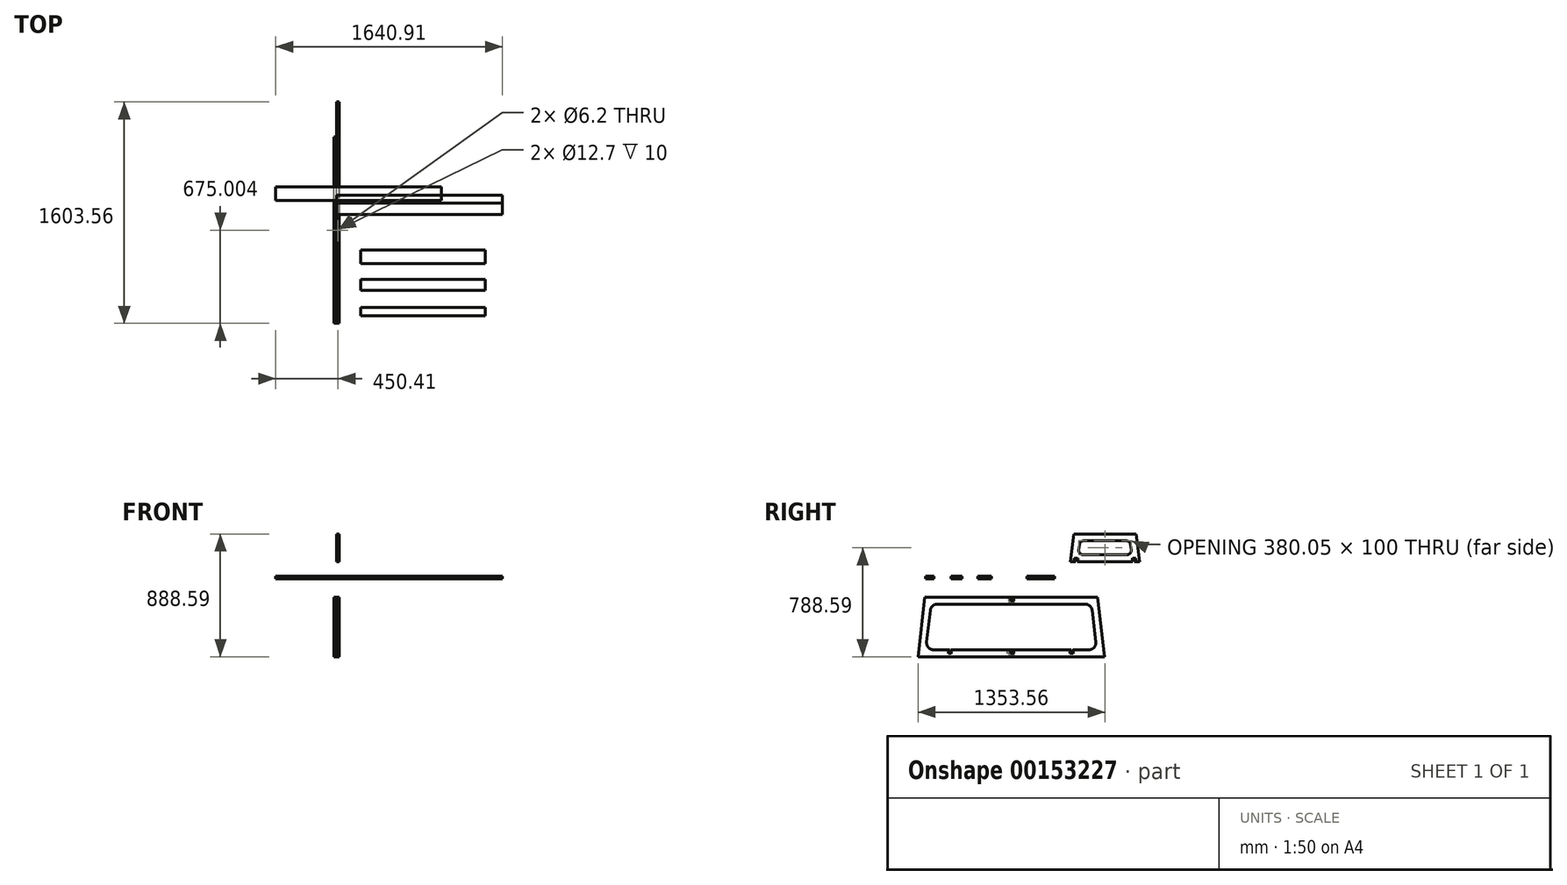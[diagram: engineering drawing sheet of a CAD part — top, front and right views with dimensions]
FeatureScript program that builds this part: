
annotation { "Feature Type Name" : "Feature", "Feature Type Description" : "" }
export const myFeature = defineFeature(function(context is Context, id is Id, definition is map)
    precondition{}
    {
        {
            var Q0;
            Q0=qCreatedBy(makeId("Top.planeOp"),FACE);
            var sketch = newSketch(context, id + "F0", { "sketchPlane" : qUnion([Q0])});
            skLineSegment(sketch, "E0.bottom", {"start": v(0, 0) * mm, "end": v(1200, 0) * mm});
            skLineSegment(sketch, "E0.top", {"start": v(0, 60) * mm, "end": v(1200, 60) * mm});
            skLineSegment(sketch, "E0.left", {"start": v(0, 0) * mm, "end": v(0, 60) * mm});
            skLineSegment(sketch, "E0.right", {"start": v(1200, 0) * mm, "end": v(1200, 60) * mm});
            skSolve(sketch);
        }
        {
            var Q0;
            Q0=makeQuery(id+"F0.imprint","IMPRINT",FACE,{"disambiguationData":[TD([[makeQuery(id+"F0.imprint","IMPRINT",EDGE,{"derivedFrom":sQuery(id+"F0.wireOp",EDGE,"E0.bottom")}),1.0]])]});
            extrude(context, id + "F1", {"entities" : qUnion([Q0]), "depth" : 19 * mm});
        }
        {
            var Q0;
            Q0=qCreatedBy(makeId("Top.planeOp"),FACE);
            var sketch = newSketch(context, id + "F2", { "sketchPlane" : qUnion([Q0])});
            skLineSegment(sketch, "E1.bottom", {"start": v(0, 0) * mm, "end": v(1200, 0) * mm});
            skLineSegment(sketch, "E1.top", {"start": v(0, -80) * mm, "end": v(1200, -80) * mm});
            skLineSegment(sketch, "E1.left", {"start": v(0, 0) * mm, "end": v(0, -80) * mm});
            skLineSegment(sketch, "E1.right", {"start": v(1200, 0) * mm, "end": v(1200, -80) * mm});
            skSolve(sketch);
        }
        {
            var Q0;
            Q0=makeQuery(id+"F2.imprint","IMPRINT",FACE,{"disambiguationData":[TD([[makeQuery(id+"F2.imprint","IMPRINT",EDGE,{"derivedFrom":sQuery(id+"F2.wireOp",EDGE,"E1.bottom")}),-1.0]])]});
            extrude(context, id + "F3", {"entities" : qUnion([Q0]), "depth" : 19 * mm});
        }
        {
            var Q0;
            Q0=qCreatedBy(makeId("Top.planeOp"),FACE);
            var sketch = newSketch(context, id + "F4", { "sketchPlane" : qUnion([Q0])});
            skLineSegment(sketch, "E2.bottom", {"start": v(-440.91, 119.85) * mm, "end": v(759.09, 119.85) * mm});
            skLineSegment(sketch, "E2.top", {"start": v(-440.91, 19.85) * mm, "end": v(759.09, 19.85) * mm});
            skLineSegment(sketch, "E2.left", {"start": v(-440.91, 119.85) * mm, "end": v(-440.91, 19.85) * mm});
            skLineSegment(sketch, "E2.right", {"start": v(759.09, 119.85) * mm, "end": v(759.09, 19.85) * mm});
            skSolve(sketch);
        }
        {
            var Q0;
            Q0=makeQuery(id+"F4.imprint","IMPRINT",FACE,{"disambiguationData":[TD([[makeQuery(id+"F4.imprint","IMPRINT",EDGE,{"derivedFrom":sQuery(id+"F4.wireOp",EDGE,"E2.bottom")}),-1.0]])]});
            extrude(context, id + "F5", {"entities" : qUnion([Q0]), "depth" : 19 * mm});
        }
        {
            var Q0;
            Q0=qCreatedBy(makeId("Right.planeOp"),FACE);
            var sketch = newSketch(context, id + "F6", { "sketchPlane" : qUnion([Q0])});
            skLineSegment(sketch, "E3", {"start": v(-819.63, -132.58) * mm, "end": v(430.37, -132.58) * mm});
            skLineSegment(sketch, "E4", {"start": v(430.37, -132.58) * mm, "end": v(480.37, -562.58) * mm});
            skLineSegment(sketch, "E5", {"start": v(480.37, -562.58) * mm, "end": v(-869.63, -562.58) * mm});
            skLineSegment(sketch, "E6", {"start": v(-869.63, -562.58) * mm, "end": v(-819.63, -132.58) * mm});
            skLineSegment(sketch, "E7.0", {"start": v(-730.58, -182.58) * mm, "end": v(341.33, -182.58) * mm});
            skLineSegment(sketch, "E7.1", {"start": v(-807, -456.8) * mm, "end": v(-780.25, -226.8) * mm});
            skLineSegment(sketch, "E7.2", {"start": v(368.07, -512.58) * mm, "end": v(-757.32, -512.58) * mm});
            skLineSegment(sketch, "E7.3", {"start": v(391, -226.8) * mm, "end": v(417.74, -456.8) * mm});
            skPoint(sketch, "E8.visualSharp", {"position": v(-775.1, -182.58) * mm});
            skArc(sketch, "E8.filletArc", {"start": v(-730.58, -182.58) * mm, "mid": v(-763.83, -195.24) * mm, "end": v(-780.25, -226.8) * mm});
            skPoint(sketch, "E9.visualSharp", {"position": v(385.85, -182.58) * mm});
            skArc(sketch, "E9.filletArc", {"start": v(391, -226.8) * mm, "mid": v(374.58, -195.24) * mm, "end": v(341.33, -182.58) * mm});
            skPoint(sketch, "E10.visualSharp", {"position": v(424.22, -512.58) * mm});
            skArc(sketch, "E10.filletArc", {"start": v(368.07, -512.58) * mm, "mid": v(405.41, -495.83) * mm, "end": v(417.74, -456.8) * mm});
            skPoint(sketch, "E11.visualSharp", {"position": v(-813.48, -512.58) * mm});
            skArc(sketch, "E11.filletArc", {"start": v(-807, -456.8) * mm, "mid": v(-794.67, -495.83) * mm, "end": v(-757.32, -512.58) * mm});
            skSolve(sketch);
        }
        {
            var Q0;
            Q0=makeQuery(id+"F6.imprint","IMPRINT",FACE,{"disambiguationData":[TD([[makeQuery(id+"F6.imprint","IMPRINT",EDGE,{"derivedFrom":sQuery(id+"F6.wireOp",EDGE,"E3")}),-1.0]])]});
            extrude(context, id + "F7", {"entities" : qUnion([Q0]), "depth" : 19 * mm});
        }
        {
            var Q0;
            Q0 = qSketchRegion(id + "F6", true);
            extrude(context, id + "F8", {"entities" : qUnion([Q0]), "oppositeDirection" : true, "depth" : 19 * mm});
        }
        {
            var Q0;
            Q0=makeQuery(id+"F7.opExtrude","SWEPT_FACE",FACE,{"disambiguationData":[OSD([sQuery(id+"F6.wireOp",EDGE,"E3")])]});
            var sketch = newSketch(context, id + "F9", { "sketchPlane" : qUnion([Q0])});
            skLineSegment(sketch, "E12", {"start": v(-59.98, -230.03) * mm, "end": v(45, -159.22) * mm});
            skLineSegment(sketch, "E13", {"start": v(45, -159.22) * mm, "end": v(55.63, -174.97) * mm});
            skLineSegment(sketch, "E14", {"start": v(55.63, -174.97) * mm, "end": v(-53.9, -248.85) * mm});
            skLineSegment(sketch, "E15", {"start": v(-53.9, -248.85) * mm, "end": v(-59.98, -230.03) * mm});
            skLineSegment(sketch, "E16", {"start": v(19, -176.76) * mm, "end": v(78.43, -176.76) * mm, "construction": true});
            skLineSegment(sketch, "E17", {"start": v(0, -212.5) * mm, "end": v(81.3, -212.5) * mm, "construction": true});
            skPoint(sketch, "E18", {"position": v(9.5, -194.63) * mm});
            skPoint(sketch, "E18.positionSnap0", {"position": v(-7.49, -194.63) * mm});
            skSolve(sketch);
        }
        {
            var Q0;
            {var subQ0=sQuery(id+"F9.wireOp",EDGE,"E12");var subQ1=sQuery(id+"F6.wireOp",EDGE,"E3");var subQ2=makeQuery(id+"F7.opExtrude","CAP_EDGE",EDGE,{"disambiguationData":[OSD([subQ1])],"isStart":true});var subQ3=makeQuery(id+"F9.imprint","INTERSECT",VERTEX,{"derivedFrom":[subQ2,subQ0]});Q0=makeQuery(id+"F9.imprint","IMPRINT",FACE,{"disambiguationData":[TD([[makeQuery(id+"F9.imprint","IMPRINT",EDGE,{"disambiguationData":[TD([[subQ3,-1.0]])],"derivedFrom":subQ0}),-1.0]])]});}
            extrude(context, id + "F10", {"entities" : qUnion([Q0]), "operationType" : NewBodyOperationType.REMOVE, "oppositeDirection" : true, "depth" : 25 * mm});
        }
        {
            var Q0;
            Q0=makeQuery(id+"F7.opExtrude","SWEPT_FACE",FACE,{"disambiguationData":[OSD([sQuery(id+"F6.wireOp",EDGE,"E7.2")])]});
            var sketch = newSketch(context, id + "F11", { "sketchPlane" : qUnion([Q0])});
            skLineSegment(sketch, "E19", {"start": v(-59.98, -227.93) * mm, "end": v(45, -157.12) * mm});
            skLineSegment(sketch, "E20", {"start": v(45, -157.12) * mm, "end": v(55.63, -172.87) * mm});
            skLineSegment(sketch, "E21", {"start": v(55.63, -172.87) * mm, "end": v(-53.9, -246.75) * mm});
            skLineSegment(sketch, "E22", {"start": v(-53.9, -246.75) * mm, "end": v(-59.98, -227.93) * mm});
            skLineSegment(sketch, "E23", {"start": v(19, -174.66) * mm, "end": v(104.14, -174.66) * mm, "construction": true});
            skLineSegment(sketch, "E24", {"start": v(0, -210.4) * mm, "end": v(81.3, -210.4) * mm, "construction": true});
            skPoint(sketch, "E25", {"position": v(9.5, -192.53) * mm});
            skPoint(sketch, "E25.positionSnap0", {"position": v(-7.49, -192.53) * mm});
            skSolve(sketch);
        }
        {
            var Q0;
            Q0 = qSketchRegion(id + "F11", true);
            extrude(context, id + "F12", {"entities" : qUnion([Q0]), "operationType" : NewBodyOperationType.REMOVE, "oppositeDirection" : true, "depth" : 25 * mm});
        }
        {
            var Q0;
            Q0=makeQuery(id+"F8.opExtrude","SWEPT_FACE",FACE,{"disambiguationData":[OSD([sQuery(id+"F6.wireOp",EDGE,"E5")])]});
            var sketch = newSketch(context, id + "F13", { "sketchPlane" : qUnion([Q0])});
            skLineSegment(sketch, "E26", {"start": v(-78.98, 159.22) * mm, "end": v(26, 230.03) * mm});
            skLineSegment(sketch, "E27", {"start": v(26, 230.03) * mm, "end": v(36.63, 214.28) * mm});
            skLineSegment(sketch, "E28", {"start": v(36.63, 214.28) * mm, "end": v(-72.9, 140.4) * mm});
            skLineSegment(sketch, "E29", {"start": v(-72.9, 140.4) * mm, "end": v(-78.98, 159.22) * mm});
            skLineSegment(sketch, "E30", {"start": v(0, 212.5) * mm, "end": v(199.93, 212.5) * mm, "construction": true});
            skLineSegment(sketch, "E31", {"start": v(-19, 176.76) * mm, "end": v(206.75, 176.76) * mm, "construction": true});
            skPoint(sketch, "E32", {"position": v(-9.5, 194.63) * mm});
            skPoint(sketch, "E32.positionSnap0", {"position": v(-26.49, 194.63) * mm});
            skSolve(sketch);
        }
        {
            var Q0;
            {var subQ0=sQuery(id+"F13.wireOp",EDGE,"016648c7-12cd-486c-9a25-a43fcb7e1467");var subQ1=sQuery(id+"F6.wireOp",EDGE,"E5");var subQ2=makeQuery(id+"F8.opExtrude","CAP_EDGE",EDGE,{"disambiguationData":[OSD([subQ1])],"isStart":false});var subQ3=makeQuery(id+"F13.imprint","INTERSECT",VERTEX,{"derivedFrom":[subQ2,subQ0]});Q0=makeQuery(id+"F13.imprint","IMPRINT",FACE,{"disambiguationData":[TD([[makeQuery(id+"F13.imprint","IMPRINT",EDGE,{"disambiguationData":[TD([[subQ3,-1.0]])],"derivedFrom":subQ0}),-1.0]])]});}
            var Q1;
            {var subQ0=sQuery(id+"F13.wireOp",EDGE,"E26");var subQ1=sQuery(id+"F6.wireOp",EDGE,"E5");var subQ2=makeQuery(id+"F8.opExtrude","CAP_EDGE",EDGE,{"disambiguationData":[OSD([subQ1])],"isStart":false});var subQ3=makeQuery(id+"F13.imprint","INTERSECT",VERTEX,{"derivedFrom":[subQ2,subQ0]});Q1=makeQuery(id+"F13.imprint","IMPRINT",FACE,{"disambiguationData":[TD([[makeQuery(id+"F13.imprint","IMPRINT",EDGE,{"disambiguationData":[TD([[subQ3,-1.0]])],"derivedFrom":subQ0}),-1.0]])]});}
            extrude(context, id + "F14", {"entities" : qUnion([Q0, Q1]), "operationType" : NewBodyOperationType.REMOVE, "oppositeDirection" : true, "depth" : 25 * mm});
        }
        {
            var Q0;
            Q0=makeQuery(id+"F8.opExtrude","SWEPT_FACE",FACE,{"disambiguationData":[OSD([sQuery(id+"F6.wireOp",EDGE,"E7.0")])]});
            var sketch = newSketch(context, id + "F15", { "sketchPlane" : qUnion([Q0])});
            skLineSegment(sketch, "E33", {"start": v(-78.98, 159.22) * mm, "end": v(26, 230.03) * mm});
            skLineSegment(sketch, "E34", {"start": v(26, 230.03) * mm, "end": v(36.63, 214.28) * mm});
            skLineSegment(sketch, "E35", {"start": v(36.63, 214.28) * mm, "end": v(-72.9, 140.4) * mm});
            skLineSegment(sketch, "E36", {"start": v(-72.9, 140.4) * mm, "end": v(-78.98, 159.22) * mm});
            skLineSegment(sketch, "E37", {"start": v(-40.65, 212.5) * mm, "end": v(0, 212.5) * mm, "construction": true});
            skLineSegment(sketch, "E38", {"start": v(-37.66, 176.76) * mm, "end": v(-19, 176.76) * mm, "construction": true});
            skPoint(sketch, "E39", {"position": v(-9.5, 194.63) * mm});
            skPoint(sketch, "E39.positionSnap0", {"position": v(-26.49, 194.63) * mm});
            skSolve(sketch);
        }
        {
            var Q0;
            {var subQ0=sQuery(id+"F15.wireOp",EDGE,"9352b724-c403-4dff-b062-4e1158279c86");var subQ1=sQuery(id+"F6.wireOp",EDGE,"E7.0");var subQ2=makeQuery(id+"F8.opExtrude","CAP_EDGE",EDGE,{"disambiguationData":[OSD([subQ1])],"isStart":false});var subQ3=makeQuery(id+"F15.imprint","INTERSECT",VERTEX,{"derivedFrom":[subQ2,subQ0]});Q0=makeQuery(id+"F15.imprint","IMPRINT",FACE,{"disambiguationData":[TD([[makeQuery(id+"F15.imprint","IMPRINT",EDGE,{"disambiguationData":[TD([[subQ3,-1.0]])],"derivedFrom":subQ0}),-1.0]])]});}
            var Q1;
            {var subQ0=sQuery(id+"F15.wireOp",EDGE,"E33");var subQ1=sQuery(id+"F6.wireOp",EDGE,"E7.0");var subQ2=makeQuery(id+"F8.opExtrude","CAP_EDGE",EDGE,{"disambiguationData":[OSD([subQ1])],"isStart":false});var subQ3=makeQuery(id+"F15.imprint","INTERSECT",VERTEX,{"derivedFrom":[subQ2,subQ0]});Q1=makeQuery(id+"F15.imprint","IMPRINT",FACE,{"disambiguationData":[TD([[makeQuery(id+"F15.imprint","IMPRINT",EDGE,{"disambiguationData":[TD([[subQ3,-1.0]])],"derivedFrom":subQ0}),-1.0]])]});}
            extrude(context, id + "F16", {"entities" : qUnion([Q0, Q1]), "operationType" : NewBodyOperationType.REMOVE, "oppositeDirection" : true, "depth" : 25 * mm});
        }
        {
            var Q0;
            {var subQ10=sQuery(id+"F6.wireOp",EDGE,"E4");var subQ11=sQuery(id+"F6.wireOp",EDGE,"E3");Q0=makeQuery(id+"F10.boolean.opBoolean","SPLIT",FACE,{"disambiguationData":[TD([makeQuery(id+"F7.opExtrude","SWEPT_FACE",FACE,{"disambiguationData":[OSD([subQ10])]})])],"derivedFrom":makeQuery(id+"F7.opExtrude","SWEPT_FACE",FACE,{"disambiguationData":[OSD([subQ11])]})});}
            var sketch = newSketch(context, id + "F17", { "sketchPlane" : qUnion([Q0])});
            skLineSegment(sketch, "E40", {"start": v(0, -212.99) * mm, "end": v(19, -176.76) * mm});
            skSolve(sketch);
        }
        {
            var Q0;
            Q0=makeQuery(id+"F7.opExtrude","SWEPT_FACE",FACE,{"disambiguationData":[OSD([sQuery(id+"F6.wireOp",EDGE,"E5")])]});
            var sketch = newSketch(context, id + "F18", { "sketchPlane" : qUnion([Q0])});
            skCircle(sketch, "E41", {"center": v(9.5, 194.63) * mm, "radius": 6.35 * mm});
            skSolve(sketch);
        }
        {
            var Q0;
            Q0=makeQuery(id+"F18.imprint","IMPRINT",FACE,{"disambiguationData":[TD([[makeQuery(id+"F18.imprint","IMPRINT",EDGE,{"derivedFrom":sQuery(id+"F18.wireOp",EDGE,"E41")}),1.0]])]});
            extrude(context, id + "F19", {"entities" : qUnion([Q0]), "operationType" : NewBodyOperationType.REMOVE, "oppositeDirection" : true, "depth" : 10 * mm});
        }
        {
            var Q0;
            Q0=makeQuery(id+"F19.boolean.opBoolean","COPY",FACE,{"derivedFrom":makeQuery(id+"F19.opExtrude","CAP_FACE",FACE,{"disambiguationData":[OSD([sQuery(id+"F18.wireOp",EDGE,"E41")])],"isStart":false})});
            var sketch = newSketch(context, id + "F20", { "sketchPlane" : qUnion([Q0])});
            skCircle(sketch, "E42", {"center": v(9.5, 194.63) * mm, "radius": 3.1 * mm});
            skSolve(sketch);
        }
        {
            var Q0;
            Q0=makeQuery(id+"F20.imprint","IMPRINT",FACE,{"disambiguationData":[TD([[makeQuery(id+"F20.imprint","IMPRINT",EDGE,{"derivedFrom":sQuery(id+"F20.wireOp",EDGE,"E42")}),1.0]])]});
            extrude(context, id + "F21", {"entities" : qUnion([Q0]), "operationType" : NewBodyOperationType.REMOVE, "endBound" : BoundingType.THROUGH_ALL, "oppositeDirection" : true, "depth" : 25 * mm});
        }
        {
            var Q0;
            Q0=makeQuery(id+"F7.opExtrude","SWEPT_FACE",FACE,{"disambiguationData":[OSD([sQuery(id+"F6.wireOp",EDGE,"E7.0")])]});
            var sketch = newSketch(context, id + "F22", { "sketchPlane" : qUnion([Q0])});
            skCircle(sketch, "E43", {"center": v(9.5, 194.63) * mm, "radius": 6.35 * mm});
            skSolve(sketch);
        }
        {
            var Q0;
            Q0=makeQuery(id+"F22.imprint","IMPRINT",FACE,{"disambiguationData":[TD([[makeQuery(id+"F22.imprint","IMPRINT",EDGE,{"derivedFrom":makeQuery(id+"F21.boolean.opBoolean","INTERSECT",EDGE,{"derivedFrom":[makeQuery(id+"F7.opExtrude","SWEPT_FACE",FACE,{"disambiguationData":[OSD([sQuery(id+"F6.wireOp",EDGE,"E7.0")])]}),makeQuery(id+"F21.opExtrude","SWEPT_FACE",FACE,{"disambiguationData":[OSD([sQuery(id+"F20.wireOp",EDGE,"E42")])]})]})}),-1.0]])]});
            extrude(context, id + "F23", {"entities" : qUnion([Q0]), "operationType" : NewBodyOperationType.REMOVE, "oppositeDirection" : true, "depth" : 10 * mm});
        }
        {
            var Q0;
            Q0=makeQuery(id+"F7.opExtrude","SWEPT_FACE",FACE,{"disambiguationData":[OSD([sQuery(id+"F6.wireOp",EDGE,"E7.0")])]});
            var sketch = newSketch(context, id + "F24", { "sketchPlane" : qUnion([Q0])});
            skCircle(sketch, "E44", {"center": v(9.5, 194.63) * mm, "radius": 6.35 * mm});
            skSolve(sketch);
        }
        {
            var Q0;
            Q0=makeQuery(id+"F24.imprint","IMPRINT",FACE,{"disambiguationData":[TD([[makeQuery(id+"F24.imprint","IMPRINT",EDGE,{"derivedFrom":sQuery(id+"F24.wireOp",EDGE,"E44")}),1.0]])]});
            extrude(context, id + "F25", {"entities" : qUnion([Q0]), "operationType" : NewBodyOperationType.REMOVE, "oppositeDirection" : true, "depth" : 10 * mm});
        }
        {
            var Q0;
            {var subQ0=sQuery(id+"F6.wireOp",EDGE,"E11.filletArc");var subQ5=sQuery(id+"F6.wireOp",EDGE,"E7.2");Q0=makeQuery(id+"F12.boolean.opBoolean","SPLIT",FACE,{"disambiguationData":[TD([makeQuery(id+"F7.opExtrude","SWEPT_FACE",FACE,{"disambiguationData":[OSD([subQ0])]})])],"derivedFrom":makeQuery(id+"F7.opExtrude","SWEPT_FACE",FACE,{"disambiguationData":[OSD([subQ5])]})});}
            var sketch = newSketch(context, id + "F26", { "sketchPlane" : qUnion([Q0])});
            skLineSegment(sketch, "E45", {"start": v(-107.43, -194.63) * mm, "end": v(150.28, -194.63) * mm, "construction": true});
            skLineSegment(sketch, "E46", {"start": v(0, -640.93) * mm, "end": v(87.61, -686.89) * mm});
            skLineSegment(sketch, "E47", {"start": v(87.61, -686.89) * mm, "end": v(87.61, -665.43) * mm});
            skLineSegment(sketch, "E48", {"start": v(87.61, -665.43) * mm, "end": v(0, -619.47) * mm});
            skLineSegment(sketch, "E49.MirrorCS", {"start": v(0, -619.47) * mm, "end": v(0, -640.93) * mm});
            skLineSegment(sketch, "E50.MirrorCS", {"start": v(-87.61, -686.89) * mm, "end": v(-87.61, -665.43) * mm});
            skLineSegment(sketch, "E51.MirrorCS", {"start": v(0, -640.93) * mm, "end": v(-87.61, -686.89) * mm});
            skLineSegment(sketch, "E52.MirrorCS", {"start": v(-87.61, -665.43) * mm, "end": v(0, -619.47) * mm});
            skLineSegment(sketch, "E53", {"start": v(0, 240.19) * mm, "end": v(19, 230.22) * mm});
            skLineSegment(sketch, "E54", {"start": v(19, 230.22) * mm, "end": v(19, 251.67) * mm});
            skLineSegment(sketch, "E55", {"start": v(19, 251.67) * mm, "end": v(0, 261.64) * mm});
            skLineSegment(sketch, "E56", {"start": v(0, 261.64) * mm, "end": v(0, 240.19) * mm});
            skLineSegment(sketch, "E57.MirrorCS", {"start": v(0, 240.19) * mm, "end": v(-19, 230.22) * mm});
            skLineSegment(sketch, "E58.MirrorCS", {"start": v(-19, 230.22) * mm, "end": v(-19, 251.67) * mm});
            skLineSegment(sketch, "E59.MirrorCS", {"start": v(-19, 251.67) * mm, "end": v(0, 261.64) * mm});
            skSolve(sketch);
        }
        {
            var Q0;
            {var subQ0=sQuery(id+"F26.wireOp",EDGE,"E49.MirrorCS");Q0=makeQuery(id+"F26.imprint","IMPRINT",FACE,{"disambiguationData":[TD([[makeQuery(id+"F26.imprint","IMPRINT",EDGE,{"derivedFrom":subQ0}),1.0]])]});}
            var Q1;
            Q1=makeQuery(id+"F26.imprint","IMPRINT",FACE,{"disambiguationData":[TD([[makeQuery(id+"F26.imprint","IMPRINT",EDGE,{"derivedFrom":sQuery(id+"F26.wireOp",EDGE,"E49.MirrorCS")}),-1.0]])]});
            var Q2;
            Q2=makeQuery(id+"F26.imprint","IMPRINT",FACE,{"disambiguationData":[TD([[makeQuery(id+"F26.imprint","IMPRINT",EDGE,{"derivedFrom":sQuery(id+"F26.wireOp",EDGE,"2f95e140-511c-4ea7-a172-9d6a93734e220.MirrorCS")}),1.0]])]});
            var Q3;
            Q3=makeQuery(id+"F26.imprint","IMPRINT",FACE,{"disambiguationData":[TD([[makeQuery(id+"F26.imprint","IMPRINT",EDGE,{"derivedFrom":sQuery(id+"F26.wireOp",EDGE,"2f95e140-511c-4ea7-a172-9d6a93734e220.MirrorCS")}),-1.0]])]});
            var Q4;
            Q4=makeQuery(id+"F26.imprint","IMPRINT",FACE,{"disambiguationData":[TD([[makeQuery(id+"F26.imprint","IMPRINT",EDGE,{"derivedFrom":sQuery(id+"F26.wireOp",EDGE,"QoEydEPh-ZxpT-TiTv-OAx2-PdRZWPOXNuFj")}),1.0]])]});
            var Q5;
            Q5=makeQuery(id+"F26.imprint","IMPRINT",FACE,{"disambiguationData":[TD([[makeQuery(id+"F26.imprint","IMPRINT",EDGE,{"derivedFrom":sQuery(id+"F26.wireOp",EDGE,"E53")}),1.0]])]});
            extrude(context, id + "F27", {"entities" : qUnion([Q0, Q1, Q2, Q3, Q4, Q5]), "operationType" : NewBodyOperationType.REMOVE, "oppositeDirection" : true, "depth" : 25 * mm});
        }
        {
            var Q0;
            Q0 = qSketchRegion(id + "F26", true);
            extrude(context, id + "F28", {"entities" : qUnion([Q0]), "operationType" : NewBodyOperationType.REMOVE, "oppositeDirection" : true, "depth" : 25 * mm});
        }
        {
            var Q0;
            Q0=qCreatedBy(makeId("Right.planeOp"),FACE);
            var sketch = newSketch(context, id + "F29", { "sketchPlane" : qUnion([Q0])});
            skLineSegment(sketch, "E60", {"start": v(233.93, 126) * mm, "end": v(733.93, 126) * mm});
            skLineSegment(sketch, "E61", {"start": v(733.93, 126) * mm, "end": v(710.69, 326) * mm});
            skLineSegment(sketch, "E62", {"start": v(710.69, 326) * mm, "end": v(257.18, 326) * mm});
            skLineSegment(sketch, "E63", {"start": v(257.18, 326) * mm, "end": v(233.93, 126) * mm});
            skLineSegment(sketch, "E64.0", {"start": v(639.45, 276) * mm, "end": v(328.42, 276) * mm});
            skLineSegment(sketch, "E64.1", {"start": v(673.9, 209.47) * mm, "end": v(669.25, 249.47) * mm});
            skLineSegment(sketch, "E64.2", {"start": v(323.77, 176) * mm, "end": v(644.1, 176) * mm});
            skLineSegment(sketch, "E64.3", {"start": v(298.62, 249.47) * mm, "end": v(293.97, 209.47) * mm});
            skPoint(sketch, "E65.visualSharp", {"position": v(301.7, 276) * mm});
            skArc(sketch, "E65.filletArc", {"start": v(328.42, 276) * mm, "mid": v(308.47, 268.41) * mm, "end": v(298.62, 249.47) * mm});
            skPoint(sketch, "E66.visualSharp", {"position": v(666.16, 276) * mm});
            skArc(sketch, "E66.filletArc", {"start": v(669.25, 249.47) * mm, "mid": v(659.4, 268.41) * mm, "end": v(639.45, 276) * mm});
            skPoint(sketch, "E67.visualSharp", {"position": v(677.79, 176) * mm});
            skArc(sketch, "E67.filletArc", {"start": v(644.1, 176) * mm, "mid": v(666.5, 186.06) * mm, "end": v(673.9, 209.47) * mm});
            skPoint(sketch, "E68.visualSharp", {"position": v(290.08, 176) * mm});
            skArc(sketch, "E68.filletArc", {"start": v(293.97, 209.47) * mm, "mid": v(301.37, 186.06) * mm, "end": v(323.77, 176) * mm});
            skSolve(sketch);
        }
        {
            var Q0;
            Q0=makeQuery(id+"F29.imprint","IMPRINT",FACE,{"disambiguationData":[TD([[makeQuery(id+"F29.imprint","IMPRINT",EDGE,{"derivedFrom":sQuery(id+"F29.wireOp",EDGE,"E60")}),1.0]])]});
            extrude(context, id + "F30", {"entities" : qUnion([Q0]), "depth" : 19 * mm});
        }
        {
            var Q0;
            Q0=makeQuery(id+"F30.opExtrude","SWEPT_FACE",FACE,{"disambiguationData":[OSD([sQuery(id+"F29.wireOp",EDGE,"E60")])]});
            var sketch = newSketch(context, id + "F31", { "sketchPlane" : qUnion([Q0])});
            skLineSegment(sketch, "E69", {"start": v(41.19, -483.93) * mm, "end": v(-21.07, -483.93) * mm, "construction": true});
            skPoint(sketch, "E69.startSnap0", {"position": v(19, -483.93) * mm});
            skPoint(sketch, "E69.endSnap0", {"position": v(0, -483.93) * mm});
            skLineSegment(sketch, "E70", {"start": v(19, -261.34) * mm, "end": v(0, -271.3) * mm});
            skLineSegment(sketch, "E71", {"start": v(0, -271.3) * mm, "end": v(0, -292.76) * mm});
            skLineSegment(sketch, "E72", {"start": v(0, -292.76) * mm, "end": v(19, -282.8) * mm});
            skLineSegment(sketch, "E73", {"start": v(19, -282.8) * mm, "end": v(19, -261.34) * mm});
            skLineSegment(sketch, "E74.MirrorCS", {"start": v(19, -685.07) * mm, "end": v(19, -706.53) * mm});
            skLineSegment(sketch, "E75.MirrorCS", {"start": v(19, -706.53) * mm, "end": v(0, -696.56) * mm});
            skLineSegment(sketch, "E76.MirrorCS", {"start": v(0, -696.56) * mm, "end": v(0, -675.1) * mm});
            skLineSegment(sketch, "E77.MirrorCS", {"start": v(0, -675.1) * mm, "end": v(19, -685.07) * mm});
            skSolve(sketch);
        }
        {
            var Q0;
            Q0=makeQuery(id+"F31.imprint","IMPRINT",FACE,{"disambiguationData":[TD([[makeQuery(id+"F31.imprint","IMPRINT",EDGE,{"derivedFrom":sQuery(id+"F31.wireOp",EDGE,"E70")}),1.0]])]});
            var Q1;
            Q1=makeQuery(id+"F31.imprint","IMPRINT",FACE,{"disambiguationData":[TD([[makeQuery(id+"F31.imprint","IMPRINT",EDGE,{"derivedFrom":sQuery(id+"F31.wireOp",EDGE,"E74.MirrorCS")}),-1.0]])]});
            extrude(context, id + "F32", {"entities" : qUnion([Q0, Q1]), "operationType" : NewBodyOperationType.REMOVE, "oppositeDirection" : true, "depth" : 25 * mm});
        }
        {
            var Q0;
            Q0=qCreatedBy(makeId("Top.planeOp"),FACE);
            var sketch = newSketch(context, id + "F33", { "sketchPlane" : qUnion([Q0])});
            skLineSegment(sketch, "E78.bottom", {"start": v(174.92, -813.17) * mm, "end": v(1074.92, -813.17) * mm});
            skLineSegment(sketch, "E78.top", {"start": v(174.92, -753.17) * mm, "end": v(1074.92, -753.17) * mm});
            skLineSegment(sketch, "E78.left", {"start": v(174.92, -813.17) * mm, "end": v(174.92, -753.17) * mm});
            skLineSegment(sketch, "E78.right", {"start": v(1074.92, -813.17) * mm, "end": v(1074.92, -753.17) * mm});
            skLineSegment(sketch, "E79.bottom", {"start": v(174.92, -630.41) * mm, "end": v(1074.92, -630.41) * mm});
            skLineSegment(sketch, "E79.top", {"start": v(174.92, -550.41) * mm, "end": v(1074.92, -550.41) * mm});
            skLineSegment(sketch, "E79.left", {"start": v(174.92, -630.41) * mm, "end": v(174.92, -550.41) * mm});
            skLineSegment(sketch, "E79.right", {"start": v(1074.92, -630.41) * mm, "end": v(1074.92, -550.41) * mm});
            skLineSegment(sketch, "E80.bottom", {"start": v(174.92, -437.31) * mm, "end": v(1074.92, -437.31) * mm});
            skLineSegment(sketch, "E80.top", {"start": v(174.92, -337.31) * mm, "end": v(1074.92, -337.31) * mm});
            skLineSegment(sketch, "E80.left", {"start": v(174.92, -437.31) * mm, "end": v(174.92, -337.31) * mm});
            skLineSegment(sketch, "E80.right", {"start": v(1074.92, -437.31) * mm, "end": v(1074.92, -337.31) * mm});
            skSolve(sketch);
        }
        {
            var Q0;
            Q0=makeQuery(id+"F33.imprint","IMPRINT",FACE,{"disambiguationData":[TD([[makeQuery(id+"F33.imprint","IMPRINT",EDGE,{"derivedFrom":sQuery(id+"F33.wireOp",EDGE,"E78.bottom")}),1.0]])]});
            extrude(context, id + "F34", {"entities" : qUnion([Q0]), "depth" : 19 * mm});
        }
        {
            var Q0;
            Q0=makeQuery(id+"F33.imprint","IMPRINT",FACE,{"disambiguationData":[TD([[makeQuery(id+"F33.imprint","IMPRINT",EDGE,{"derivedFrom":sQuery(id+"F33.wireOp",EDGE,"E79.bottom")}),1.0]])]});
            extrude(context, id + "F35", {"entities" : qUnion([Q0]), "depth" : 19 * mm});
        }
        {
            var Q0;
            Q0=makeQuery(id+"F33.imprint","IMPRINT",FACE,{"disambiguationData":[TD([[makeQuery(id+"F33.imprint","IMPRINT",EDGE,{"derivedFrom":sQuery(id+"F33.wireOp",EDGE,"E80.bottom")}),1.0]])]});
            extrude(context, id + "F36", {"entities" : qUnion([Q0]), "depth" : 19 * mm});
        }
        {
            var Q0;
            {var subQ0=sQuery(id+"F6.wireOp",EDGE,"E11.filletArc");var subQ1=sQuery(id+"F6.wireOp",EDGE,"E7.2");var subQ4=makeQuery(id+"F12.opExtrude","SWEPT_FACE",FACE,{"disambiguationData":[OSD([sQuery(id+"F11.wireOp",EDGE,"E21")])]});Q0=makeQuery(id+"F27.boolean.opBoolean","SPLIT",EDGE,{"disambiguationData":[TD([makeQuery(id+"F12.boolean.opBoolean","COPY",FACE,{"derivedFrom":subQ4})])],"derivedFrom":makeQuery(id+"F12.boolean.opBoolean","SPLIT",EDGE,{"disambiguationData":[TD([makeQuery(id+"F7.opExtrude","SWEPT_FACE",FACE,{"disambiguationData":[OSD([subQ0])]})])],"derivedFrom":makeQuery(id+"F7.opExtrude","CAP_EDGE",EDGE,{"disambiguationData":[OSD([subQ1])],"isStart":false})})});}
            var Q1;
            {var subQ0=sQuery(id+"F6.wireOp",EDGE,"E10.filletArc");var subQ1=sQuery(id+"F6.wireOp",EDGE,"E7.2");var subQ4=makeQuery(id+"F12.opExtrude","SWEPT_FACE",FACE,{"disambiguationData":[OSD([sQuery(id+"F11.wireOp",EDGE,"E19")])]});Q1=makeQuery(id+"F27.boolean.opBoolean","SPLIT",EDGE,{"disambiguationData":[TD([makeQuery(id+"F12.boolean.opBoolean","COPY",FACE,{"derivedFrom":subQ4})])],"derivedFrom":makeQuery(id+"F12.boolean.opBoolean","SPLIT",EDGE,{"disambiguationData":[TD([makeQuery(id+"F7.opExtrude","SWEPT_FACE",FACE,{"disambiguationData":[OSD([subQ0])]})])],"derivedFrom":makeQuery(id+"F7.opExtrude","CAP_EDGE",EDGE,{"disambiguationData":[OSD([subQ1])],"isStart":false})})});}
            var Q2;
            {var subQ0=sQuery(id+"F6.wireOp",EDGE,"E10.filletArc");var subQ1=sQuery(id+"F6.wireOp",EDGE,"E7.2");var subQ4=makeQuery(id+"F7.opExtrude","SWEPT_FACE",FACE,{"disambiguationData":[OSD([subQ0])]});Q2=makeQuery(id+"F27.boolean.opBoolean","SPLIT",EDGE,{"disambiguationData":[TD([subQ4])],"derivedFrom":makeQuery(id+"F12.boolean.opBoolean","SPLIT",EDGE,{"disambiguationData":[TD([subQ4])],"derivedFrom":makeQuery(id+"F7.opExtrude","CAP_EDGE",EDGE,{"disambiguationData":[OSD([subQ1])],"isStart":false})})});}
            fillet(context, id + "F37", {"entities" : qUnion([Q0, Q1, Q2]), "radius" : 5 * mm, "tangentPropagation" : true, "allowEdgeOverflow" : false});
        }
    });
